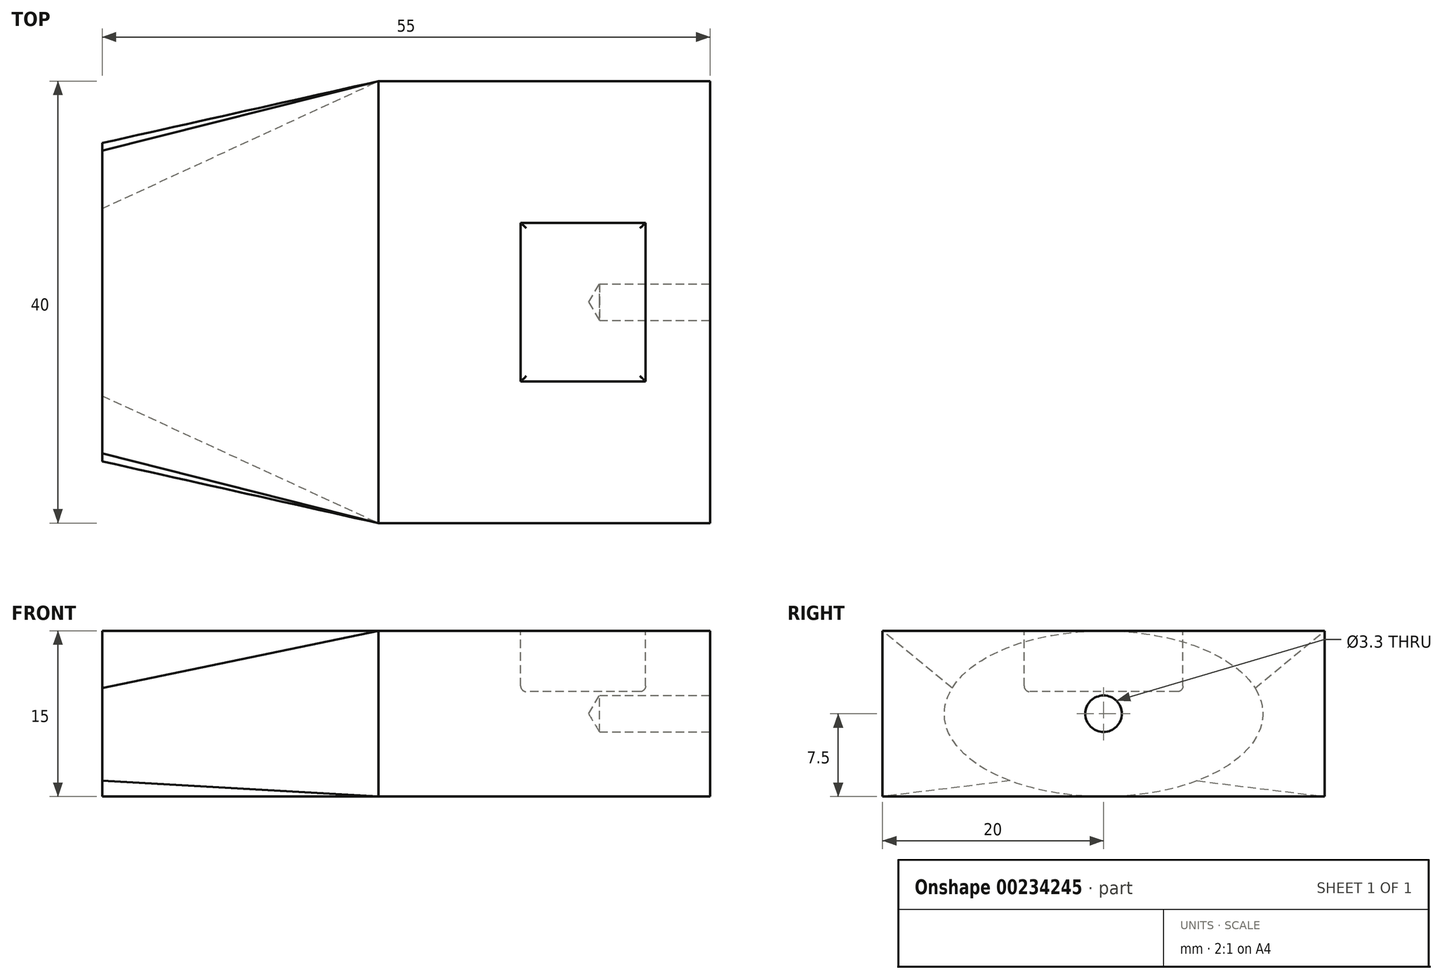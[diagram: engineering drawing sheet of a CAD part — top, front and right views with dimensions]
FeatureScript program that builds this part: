
annotation { "Feature Type Name" : "Feature", "Feature Type Description" : "" }
export const myFeature = defineFeature(function(context is Context, id is Id, definition is map)
    precondition{}
    {
        {
            var Q0;
            Q0=qCreatedBy(makeId("Top.planeOp"),FACE);
            var sketch = newSketch(context, id + "F0", { "sketchPlane" : qUnion([Q0])});
            skLineSegment(sketch, "E0.bottom", {"start": v(15, 20) * mm, "end": v(-15, 20) * mm});
            skLineSegment(sketch, "E0.top", {"start": v(15, -20) * mm, "end": v(-15, -20) * mm});
            skLineSegment(sketch, "E0.left", {"start": v(15, 20) * mm, "end": v(15, -20) * mm});
            skLineSegment(sketch, "E0.right", {"start": v(-15, 20) * mm, "end": v(-15, -20) * mm});
            skPoint(sketch, "E0.middle", {"position": v(0, 0) * mm});
            skSolve(sketch);
        }
        {
            var Q0;
            Q0 = qSketchRegion(id + "F0", true);
            extrude(context, id + "F1", {"entities" : qUnion([Q0]), "depth" : 15 * mm});
        }
        {
            var Q0;
            Q0=makeQuery(id+"F1.opExtrude","SWEPT_FACE",FACE,{"disambiguationData":[OSD([sQuery(id+"F0.wireOp",EDGE,"E0.left")])]});
            var sketch = newSketch(context, id + "F2", { "sketchPlane" : qUnion([Q0])});
            skCircle(sketch, "E1", {"center": v(0, 7.5) * mm, "radius": 3 * mm});
            skLineSegment(sketch, "E2", {"start": v(-20, 15) * mm, "end": v(20, 0) * mm, "construction": true});
            skSolve(sketch);
        }
        {
            var Q0;
            Q0=sQuery(id+"F2.wireOp",VERTEX,"E1.center");
            var Q1;
            Q1=makeQuery(id+"F1.opExtrude","SWEPT_BODY",BODY,{"disambiguationData":[OSD([sQuery(id+"F0.wireOp",EDGE,"E0.bottom"),sQuery(id+"F0.wireOp",EDGE,"E0.top"),sQuery(id+"F0.wireOp",EDGE,"E0.left"),sQuery(id+"F0.wireOp",EDGE,"E0.right")])]});
            hole(context, id + "F3", {"style" : HoleStyle.SIMPLE, "endStyle" : HoleEndStyle.BLIND, "standardTappedOrClearance" : lookupTablePath({ "standard" : "ISO", "fit" : "Normal", "engagement" : "75%", "pitch" : "0.9 mm", "size" : "M3", "type" : "Clearance" }), "standardBlindInLast" : lookupTablePath({ "fit" : "Standard", "standard" : "ISO", "engagement" : "75%", "pitch" : "0.9 mm", "size" : "M3", "type" : "Clearance" }), "holeDiameter" : 3.3 * mm, "holeDepth" : 10 * mm, "locations" : qUnion([Q0]), "scope" : qUnion([Q1])});
        }
        {
            var Q0;
            Q0=makeQuery(id+"F1.opExtrude","CAP_FACE",FACE,{"disambiguationData":[OSD([sQuery(id+"F0.wireOp",EDGE,"E0.bottom"),sQuery(id+"F0.wireOp",EDGE,"E0.top"),sQuery(id+"F0.wireOp",EDGE,"E0.left"),sQuery(id+"F0.wireOp",EDGE,"E0.right")])],"isStart":false});
            var sketch = newSketch(context, id + "F4", { "sketchPlane" : qUnion([Q0])});
            skLineSegment(sketch, "E3.bottom", {"start": v(9.16, 7.18) * mm, "end": v(-2.13, 7.18) * mm});
            skLineSegment(sketch, "E3.top", {"start": v(9.16, -7.18) * mm, "end": v(-2.13, -7.18) * mm});
            skLineSegment(sketch, "E3.left", {"start": v(9.16, 7.18) * mm, "end": v(9.16, -7.18) * mm});
            skLineSegment(sketch, "E3.right", {"start": v(-2.13, 7.18) * mm, "end": v(-2.13, -7.18) * mm});
            skPoint(sketch, "E3.middle", {"position": v(3.52, 0) * mm});
            skSolve(sketch);
        }
        {
            var Q0;
            Q0 = qSketchRegion(id + "F4", true);
            extrude(context, id + "F5", {"entities" : qUnion([Q0]), "operationType" : NewBodyOperationType.REMOVE, "oppositeDirection" : true, "depth" : 5.5 * mm});
        }
        {
            var Q0;
            Q0=makeQuery(id+"F5.boolean.opBoolean","COPY",EDGE,{"derivedFrom":makeQuery(id+"F5.opExtrude","CAP_EDGE",EDGE,{"disambiguationData":[OSD([sQuery(id+"F4.wireOp",EDGE,"E3.right")])],"isStart":false})});
            var Q1;
            Q1=makeQuery(id+"F5.boolean.opBoolean","COPY",EDGE,{"derivedFrom":makeQuery(id+"F5.opExtrude","CAP_EDGE",EDGE,{"disambiguationData":[OSD([sQuery(id+"F4.wireOp",EDGE,"E3.bottom")])],"isStart":false})});
            var Q2;
            Q2=makeQuery(id+"F5.boolean.opBoolean","COPY",EDGE,{"derivedFrom":makeQuery(id+"F5.opExtrude","CAP_EDGE",EDGE,{"disambiguationData":[OSD([sQuery(id+"F4.wireOp",EDGE,"E3.left")])],"isStart":false})});
            var Q3;
            Q3=makeQuery(id+"F5.boolean.opBoolean","COPY",EDGE,{"derivedFrom":makeQuery(id+"F5.opExtrude","CAP_EDGE",EDGE,{"disambiguationData":[OSD([sQuery(id+"F4.wireOp",EDGE,"E3.top")])],"isStart":false})});
            fillet(context, id + "F6", {"entities" : qUnion([Q0, Q1, Q2, Q3]), "radius" : 0.5 * mm, "tangentPropagation" : true, "allowEdgeOverflow" : false});
        }
        {
            var Q0;
            Q0=makeQuery(id+"F1.opExtrude","SWEPT_FACE",FACE,{"disambiguationData":[OSD([sQuery(id+"F0.wireOp",EDGE,"E0.right")])]});
            cPlane(context, id + "F7", {"entities" : qUnion([Q0]), "cplaneType" : CPlaneType.OFFSET, "offset" : 25 * mm, "width" : 150 * mm, "height" : 150 * mm});
        }
        {
            var Q0;
            Q0=qCreatedBy(id+"F7.planeOp",FACE);
            var sketch = newSketch(context, id + "F8", { "sketchPlane" : qUnion([Q0])});
            skPoint(sketch, "E4.centerSnap0", {"position": v(20, 7.5) * mm});
            skEllipse(sketch, "E5", {"center": v(0, 7.5) * mm, "majorRadius": 14.4 * mm, "minorRadius": 7.5 * mm, "majorAxis": v(-1, 0)});
            skLineSegment(sketch, "E6", {"start": v(-14.4, 7.5) * mm, "end": v(14.4, 7.5) * mm, "construction": true});
            skLineSegment(sketch, "E7", {"start": v(0, 15) * mm, "end": v(0, 0) * mm, "construction": true});
            skSolve(sketch);
        }
        {
            var Q0;
            Q0=makeQuery(id+"F1.opExtrude","SWEPT_FACE",FACE,{"disambiguationData":[OSD([sQuery(id+"F0.wireOp",EDGE,"E0.right")])]});
            var sketch = newSketch(context, id + "F9", { "sketchPlane" : qUnion([Q0])});
            skLineSegment(sketch, "E8", {"start": v(20, 7.5) * mm, "end": v(-20, 7.5) * mm, "construction": true});
            skLineSegment(sketch, "E9", {"start": v(0, 15) * mm, "end": v(0, 0) * mm, "construction": true});
            skSolve(sketch);
        }
        {
            var Q1;
            Q1=makeQuery(id+"F8.imprint","IMPRINT",FACE,{"disambiguationData":[TD([[makeQuery(id+"F8.imprint","IMPRINT",EDGE,{"derivedFrom":sQuery(id+"F8.wireOp",EDGE,"E5")}),1.0]])]});
            var Q2;
            Q2=makeQuery(id+"F1.opExtrude","SWEPT_FACE",FACE,{"disambiguationData":[OSD([sQuery(id+"F0.wireOp",EDGE,"E0.right")])]});
            var Q3;
            Q3=sQuery(id+"F8.wireOp",VERTEX,"E7.start");
            var Q4;
            Q4=sQuery(id+"F9.wireOp",VERTEX,"E9.start");
            loft(context, id + "F10", {"operationType" : NewBodyOperationType.ADD, "sheetProfilesArray" : [{ "sheetProfileEntities" : qUnion([Q1]) }, { "sheetProfileEntities" : qUnion([Q2]) }], "matchConnections" : true, "connections" : [{ "connectionEntities" : qUnion([Q3, Q4]), "connectionEdgeQueries" : qUnion([]), "connectionEdgeParameters" : [] }]});
        }
    });
